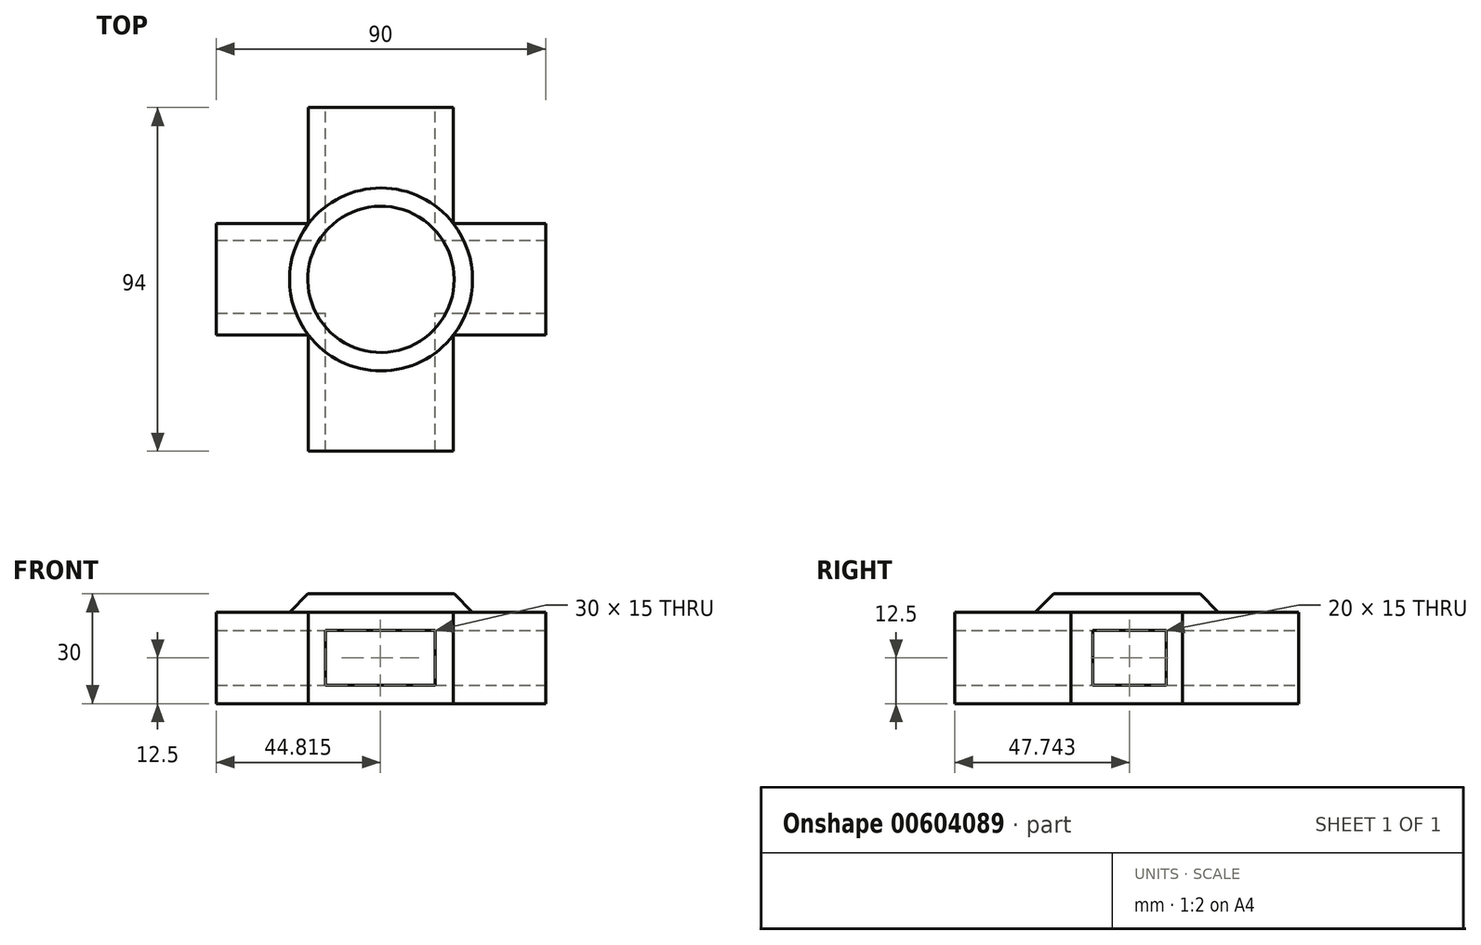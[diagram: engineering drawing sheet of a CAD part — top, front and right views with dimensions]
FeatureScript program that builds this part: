
annotation { "Feature Type Name" : "Feature", "Feature Type Description" : "" }
export const myFeature = defineFeature(function(context is Context, id is Id, definition is map)
    precondition{}
    {
        {
            var Q0;
            Q0=qCreatedBy(makeId("Top.planeOp"),FACE);
            var sketch = newSketch(context, id + "F0", { "sketchPlane" : qUnion([Q0])});
            skCircle(sketch, "E0", {"center": v(16.96, -28.3) * mm, "radius": 25 * mm});
            skLineSegment(sketch, "E1.bottom", {"start": v(61.96, -75.3) * mm, "end": v(-28.04, -75.3) * mm});
            skLineSegment(sketch, "E1.top", {"start": v(61.96, 18.7) * mm, "end": v(-28.04, 18.7) * mm});
            skLineSegment(sketch, "E1.left", {"start": v(61.96, -75.3) * mm, "end": v(61.96, 18.7) * mm});
            skLineSegment(sketch, "E1.right", {"start": v(-28.04, -75.3) * mm, "end": v(-28.04, 18.7) * mm});
            skSolve(sketch);
        }
        {
            var Q0;
            Q0=makeQuery(id+"F0.imprint","IMPRINT",FACE,{"disambiguationData":[TD([[makeQuery(id+"F0.imprint","IMPRINT",EDGE,{"derivedFrom":sQuery(id+"F0.wireOp",EDGE,"E0")}),1.0]])]});
            extrude(context, id + "F1", {"entities" : qUnion([Q0]), "depth" : 30 * mm, "offsetDistance" : 25 * mm});
        }
        {
            var Q0;
            Q0 = qSketchRegion(id + "F0", true);
            extrude(context, id + "F2", {"entities" : qUnion([Q0]), "operationType" : NewBodyOperationType.ADD, "depth" : 25 * mm, "offsetDistance" : 25 * mm});
        }
        {
            var Q0;
            Q0=makeQuery(id+"F1.opExtrude","CAP_EDGE",EDGE,{"disambiguationData":[OSD([sQuery(id+"F0.wireOp",EDGE,"E0")])],"isStart":false});
            chamfer(context, id + "F3", {"entities" : qUnion([Q0]), "width" : 5 * mm, "tangentPropagation" : true});
        }
        {
            var Q0;
            Q0=makeQuery(id+"F2.opExtrude","CAP_FACE",FACE,{"disambiguationData":[OSD([sQuery(id+"F0.wireOp",EDGE,"E0"),sQuery(id+"F0.wireOp",EDGE,"E1.bottom"),sQuery(id+"F0.wireOp",EDGE,"E1.top"),sQuery(id+"F0.wireOp",EDGE,"E1.left"),sQuery(id+"F0.wireOp",EDGE,"E1.right")])],"isStart":false});
            var sketch = newSketch(context, id + "F4", { "sketchPlane" : qUnion([Q0])});
            skLineSegment(sketch, "E2.bottom", {"start": v(61.96, 18.7) * mm, "end": v(36.78, 18.7) * mm});
            skLineSegment(sketch, "E2.top", {"start": v(61.96, -13.05) * mm, "end": v(36.78, -13.05) * mm});
            skLineSegment(sketch, "E2.left", {"start": v(61.96, 18.7) * mm, "end": v(61.96, -13.05) * mm});
            skLineSegment(sketch, "E2.right", {"start": v(36.78, 18.7) * mm, "end": v(36.78, -13.05) * mm});
            skLineSegment(sketch, "E3.bottom", {"start": v(-28.04, 18.7) * mm, "end": v(-2.85, 18.7) * mm});
            skLineSegment(sketch, "E3.top", {"start": v(-28.04, -13.05) * mm, "end": v(-2.85, -13.05) * mm});
            skLineSegment(sketch, "E3.left", {"start": v(-28.04, 18.7) * mm, "end": v(-28.04, -13.05) * mm});
            skLineSegment(sketch, "E3.right", {"start": v(-2.85, 18.7) * mm, "end": v(-2.85, -13.05) * mm});
            skLineSegment(sketch, "E4.bottom", {"start": v(61.96, -75.3) * mm, "end": v(36.78, -75.3) * mm});
            skLineSegment(sketch, "E4.top", {"start": v(61.96, -43.54) * mm, "end": v(36.78, -43.54) * mm});
            skLineSegment(sketch, "E4.left", {"start": v(61.96, -75.3) * mm, "end": v(61.96, -43.54) * mm});
            skLineSegment(sketch, "E4.right", {"start": v(36.78, -75.3) * mm, "end": v(36.78, -43.54) * mm});
            skLineSegment(sketch, "E5.bottom", {"start": v(-28.04, -75.3) * mm, "end": v(-2.85, -75.3) * mm});
            skLineSegment(sketch, "E5.top", {"start": v(-28.04, -43.54) * mm, "end": v(-2.85, -43.54) * mm});
            skLineSegment(sketch, "E5.left", {"start": v(-28.04, -75.3) * mm, "end": v(-28.04, -43.54) * mm});
            skLineSegment(sketch, "E5.right", {"start": v(-2.85, -75.3) * mm, "end": v(-2.85, -43.54) * mm});
            skSolve(sketch);
        }
        {
            var Q0;
            Q0=makeQuery(id+"F4.imprint","IMPRINT",FACE,{"disambiguationData":[TD([[makeQuery(id+"F4.imprint","IMPRINT",EDGE,{"derivedFrom":sQuery(id+"F4.wireOp",EDGE,"E2.bottom")}),1.0]])]});
            extrude(context, id + "F5", {"entities" : qUnion([Q0]), "operationType" : NewBodyOperationType.REMOVE, "oppositeDirection" : true, "depth" : 100 * mm, "offsetDistance" : 25 * mm});
        }
        {
            var Q0;
            Q0=makeQuery(id+"F4.imprint","IMPRINT",FACE,{"disambiguationData":[TD([[makeQuery(id+"F4.imprint","IMPRINT",EDGE,{"derivedFrom":sQuery(id+"F4.wireOp",EDGE,"E3.bottom")}),1.0]])]});
            var Q1;
            Q1=makeQuery(id+"F4.imprint","IMPRINT",FACE,{"disambiguationData":[TD([[makeQuery(id+"F4.imprint","IMPRINT",EDGE,{"derivedFrom":sQuery(id+"F4.wireOp",EDGE,"E5.bottom")}),-1.0]])]});
            var Q2;
            Q2=makeQuery(id+"F4.imprint","IMPRINT",FACE,{"disambiguationData":[TD([[makeQuery(id+"F4.imprint","IMPRINT",EDGE,{"derivedFrom":sQuery(id+"F4.wireOp",EDGE,"E4.bottom")}),-1.0]])]});
            extrude(context, id + "F6", {"entities" : qUnion([Q0, Q1, Q2]), "operationType" : NewBodyOperationType.REMOVE, "oppositeDirection" : true, "depth" : 100 * mm, "offsetDistance" : 25 * mm});
        }
        {
            var Q0;
            Q0=makeQuery(id+"F2.opExtrude","SWEPT_FACE",FACE,{"disambiguationData":[OSD([sQuery(id+"F0.wireOp",EDGE,"E1.top")])]});
            var sketch = newSketch(context, id + "F7", { "sketchPlane" : qUnion([Q0])});
            skLineSegment(sketch, "E6.bottom", {"start": v(-1.78, 5) * mm, "end": v(-31.78, 5) * mm});
            skLineSegment(sketch, "E6.top", {"start": v(-1.78, 20) * mm, "end": v(-31.78, 20) * mm});
            skLineSegment(sketch, "E6.left", {"start": v(-1.78, 5) * mm, "end": v(-1.78, 20) * mm});
            skLineSegment(sketch, "E6.right", {"start": v(-31.78, 5) * mm, "end": v(-31.78, 20) * mm});
            skSolve(sketch);
        }
        {
            var Q0;
            Q0=makeQuery(id+"F7.imprint","IMPRINT",FACE,{"disambiguationData":[TD([[makeQuery(id+"F7.imprint","IMPRINT",EDGE,{"derivedFrom":sQuery(id+"F7.wireOp",EDGE,"E6.bottom")}),-1.0]])]});
            extrude(context, id + "F8", {"entities" : qUnion([Q0]), "operationType" : NewBodyOperationType.REMOVE, "oppositeDirection" : true, "depth" : 1000 * mm, "offsetDistance" : 25 * mm});
        }
        {
            var Q0;
            Q0=makeQuery(id+"F2.opExtrude","SWEPT_FACE",FACE,{"disambiguationData":[OSD([sQuery(id+"F0.wireOp",EDGE,"E1.left")])]});
            var sketch = newSketch(context, id + "F9", { "sketchPlane" : qUnion([Q0])});
            skLineSegment(sketch, "E7.bottom", {"start": v(-37.55, 20) * mm, "end": v(-17.55, 20) * mm});
            skLineSegment(sketch, "E7.top", {"start": v(-37.55, 5) * mm, "end": v(-17.55, 5) * mm});
            skLineSegment(sketch, "E7.left", {"start": v(-37.55, 20) * mm, "end": v(-37.55, 5) * mm});
            skLineSegment(sketch, "E7.right", {"start": v(-17.55, 20) * mm, "end": v(-17.55, 5) * mm});
            skSolve(sketch);
        }
        {
            var Q0;
            Q0=makeQuery(id+"F9.imprint","IMPRINT",FACE,{"disambiguationData":[TD([[makeQuery(id+"F9.imprint","IMPRINT",EDGE,{"derivedFrom":sQuery(id+"F9.wireOp",EDGE,"E7.bottom")}),-1.0]])]});
            extrude(context, id + "F10", {"entities" : qUnion([Q0]), "operationType" : NewBodyOperationType.REMOVE, "oppositeDirection" : true, "depth" : 100 * mm, "offsetDistance" : 25 * mm});
        }
    });
